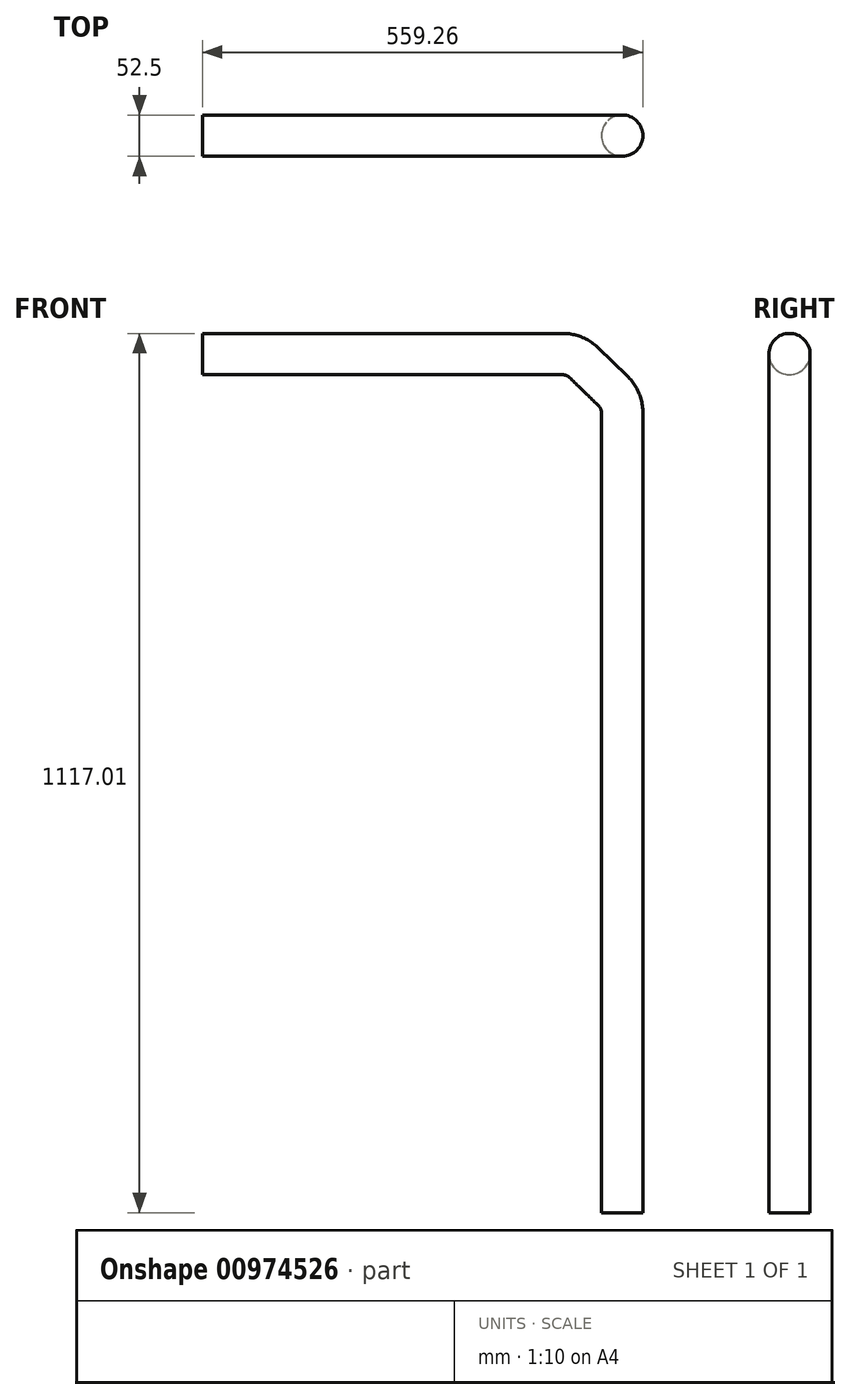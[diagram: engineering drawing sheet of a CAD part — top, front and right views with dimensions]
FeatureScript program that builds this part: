
annotation { "Feature Type Name" : "Feature", "Feature Type Description" : "" }
export const myFeature = defineFeature(function(context is Context, id is Id, definition is map)
    precondition{}
    {
        {
            var Q0;
            Q0=qCreatedBy(makeId("Right.planeOp"),FACE);
            var sketch = newSketch(context, id + "F0", { "sketchPlane" : qUnion([Q0])});
            skCircle(sketch, "E0", {"center": v(0, 0) * mm, "radius": 26.25 * mm});
            skSolve(sketch);
        }
        {
            var Q0;
            Q0=qCreatedBy(makeId("Front.planeOp"),FACE);
            var sketch = newSketch(context, id + "F1", { "sketchPlane" : qUnion([Q0])});
            skLineSegment(sketch, "E1.0", {"start": v(0, 26.25) * mm, "end": v(0, -26.25) * mm, "construction": true});
            skArc(sketch, "E2", {"start": v(0, 0) * mm, "mid": v(14.8, -2.89) * mm, "end": v(27.43, -11.13) * mm});
            skSolve(sketch);
        }
        {
            var Q0;
            Q0=makeQuery(id+"F0.imprint","IMPRINT",FACE,{"disambiguationData":[TD([[makeQuery(id+"F0.imprint","IMPRINT",EDGE,{"derivedFrom":sQuery(id+"F0.wireOp",EDGE,"E0")}),1.0]])]});
            var Q1;
            Q1=qConstructionFilter(qBodyType(qCreatedBy(id+"F1",EDGE),BodyType.WIRE),ConstructionObject.NO);
            sweep(context, id + "F2", {"profiles" : qUnion([Q0]), "path" : qUnion([Q1])});
        }
        {
            var Q0;
            Q0=makeQuery(id+"F2.opSweep","CAP_FACE",FACE,{"disambiguationData":[OSD([sQuery(id+"F1.wireOp",VERTEX,"JRzNX78w-aib6-DEKG-eYSx-uGncHlC766wC.end"),sQuery(id+"F0.wireOp",EDGE,"E0")])],"isStart":false});
            var sketch = newSketch(context, id + "F3", { "sketchPlane" : qUnion([Q0])});
            skCircle(sketch, "E3", {"center": v(0, 11.13) * mm, "radius": 26.25 * mm});
            skSolve(sketch);
        }
        {
            var Q0;
            Q0=qSketchRegion(id+"F3",true);
            extrude(context, id + "F4", {"entities" : qUnion([Q0]), "operationType" : NewBodyOperationType.ADD, "depth" : 50.8 * mm, "offsetDistance" : 25.4 * mm});
        }
        {
            var Q0;
            Q0=qCreatedBy(makeId("Front.planeOp"),FACE);
            var sketch = newSketch(context, id + "F5", { "sketchPlane" : qUnion([Q0])});
            skLineSegment(sketch, "E4.0", {"start": v(82.16, -27.69) * mm, "end": v(45.58, -65.35) * mm, "construction": true});
            skArc(sketch, "E5", {"start": v(63.87, -46.52) * mm, "mid": v(72.7, -59.43) * mm, "end": v(75.81, -74.76) * mm});
            skLineSegment(sketch, "E6", {"start": v(63.87, -46.52) * mm, "end": v(20.02, -91.68) * mm, "construction": true});
            skSolve(sketch);
        }
        {
            var Q0;
            Q0=makeQuery(id+"F4.opExtrude","CAP_FACE",FACE,{"disambiguationData":[OSD([sQuery(id+"F3.wireOp",EDGE,"E3")])],"isStart":false});
            var Q1;
            Q1=qConstructionFilter(qBodyType(qCreatedBy(id+"F5",EDGE),BodyType.WIRE),ConstructionObject.NO);
            sweep(context, id + "F6", {"operationType" : NewBodyOperationType.ADD, "profiles" : qUnion([Q0]), "path" : qUnion([Q1])});
        }
        {
            var Q0;
            Q0=makeQuery(id+"F2.opSweep","CAP_FACE",FACE,{"disambiguationData":[OSD([sQuery(id+"F1.wireOp",VERTEX,"JRzNX78w-aib6-DEKG-eYSx-uGncHlC766wC.start"),sQuery(id+"F0.wireOp",EDGE,"E0")])],"isStart":true});
            var sketch = newSketch(context, id + "F7", { "sketchPlane" : qUnion([Q0])});
            skCircle(sketch, "E7", {"center": v(0, 0) * mm, "radius": 26.25 * mm});
            skSolve(sketch);
        }
        {
            var Q0;
            Q0=qSketchRegion(id+"F7",true);
            extrude(context, id + "F8", {"entities" : qUnion([Q0]), "operationType" : NewBodyOperationType.ADD, "depth" : 457.2 * mm, "offsetDistance" : 25.4 * mm});
        }
        {
            var Q0;
            Q0=makeQuery(id+"F6.opSweep","CAP_FACE",FACE,{"disambiguationData":[OSD([sQuery(id+"F3.wireOp",EDGE,"E3"),sQuery(id+"F5.wireOp",VERTEX,"E5.end")])],"isStart":false});
            extrude(context, id + "F9", {"entities" : qUnion([Q0]), "operationType" : NewBodyOperationType.ADD, "depth" : 1016 * mm, "offsetDistance" : 25.4 * mm});
        }
    });
